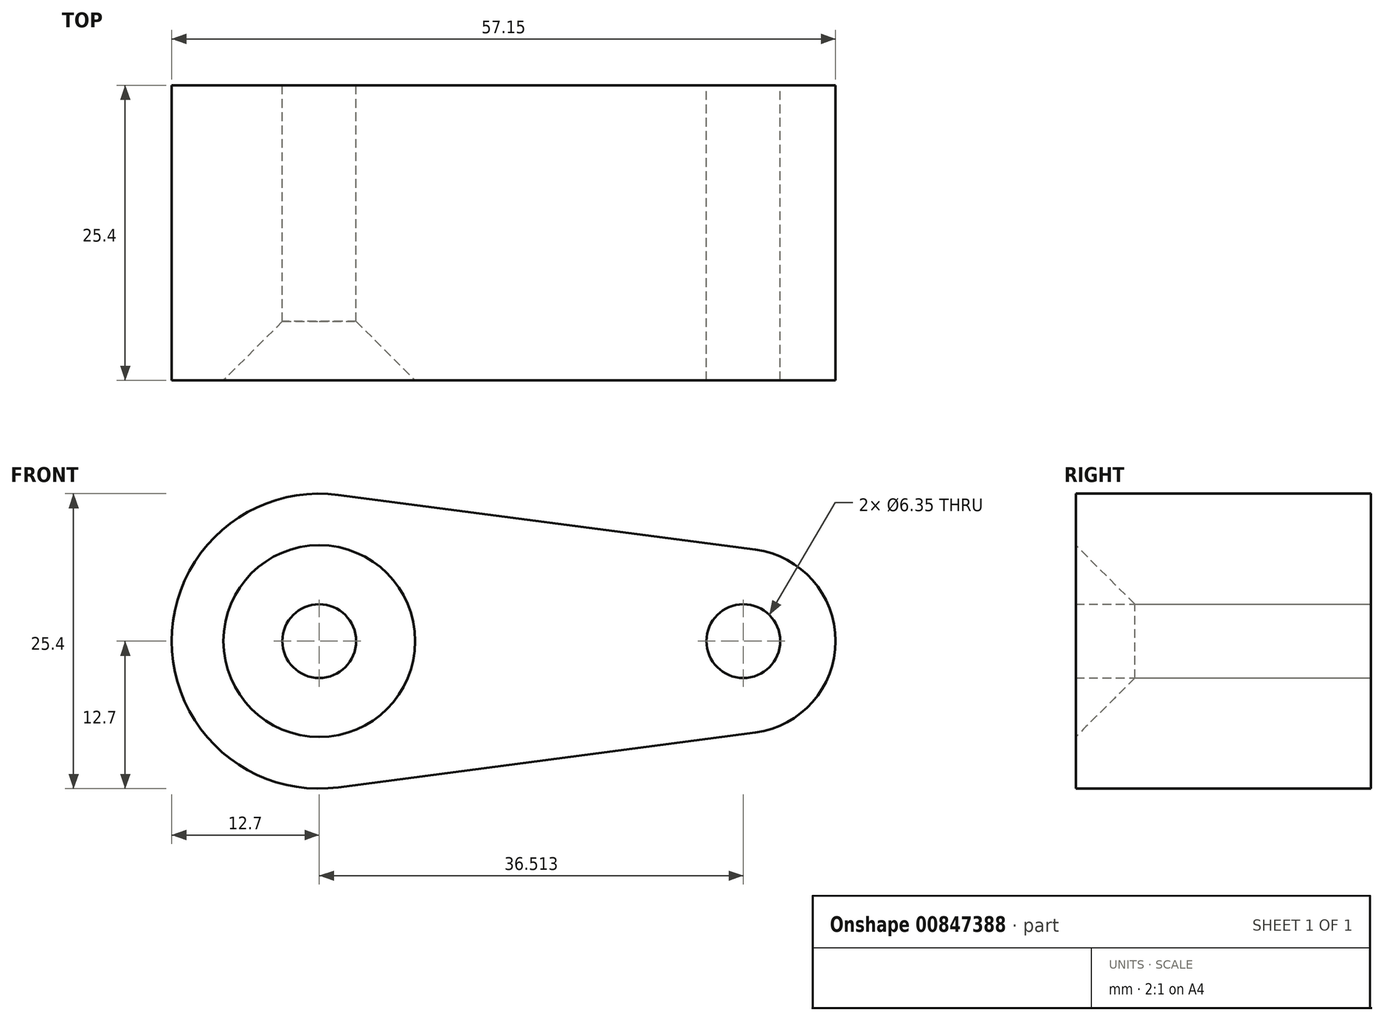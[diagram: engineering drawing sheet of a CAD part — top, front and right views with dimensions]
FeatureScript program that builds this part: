
annotation { "Feature Type Name" : "Feature", "Feature Type Description" : "" }
export const myFeature = defineFeature(function(context is Context, id is Id, definition is map)
    precondition{}
    {
        {
            var Q0;
            Q0=qCreatedBy(makeId("Front.planeOp"),FACE);
            var sketch = newSketch(context, id + "F0", { "sketchPlane" : qUnion([Q0])});
            skLineSegment(sketch, "E0.bottom", {"start": v(-46.46, 87.45) * mm, "end": v(47.03, 87.45) * mm});
            skLineSegment(sketch, "E0.top", {"start": v(-46.46, -90.1) * mm, "end": v(47.03, -90.1) * mm});
            skLineSegment(sketch, "E0.left", {"start": v(-46.46, 87.45) * mm, "end": v(-46.46, -90.1) * mm});
            skLineSegment(sketch, "E0.right", {"start": v(47.03, 87.45) * mm, "end": v(47.03, -90.1) * mm});
            skCircle(sketch, "E1", {"center": v(0, 0) * mm, "radius": 7.39 * mm});
            skSolve(sketch);
        }
        {
            var Q0;
            Q0=makeQuery(id+"F0.imprint","IMPRINT",FACE,{"disambiguationData":[TD([[makeQuery(id+"F0.imprint","IMPRINT",EDGE,{"derivedFrom":sQuery(id+"F0.wireOp",EDGE,"E0.bottom")}),-1.0]])]});
            extrude(context, id + "F1", {"entities" : qUnion([Q0]), "depth" : 25.4 * mm, "offsetDistance" : 25.4 * mm});
        }
        {
            var Q0;
            Q0=makeQuery(id+"F1.opExtrude","CAP_FACE",FACE,{"disambiguationData":[OSD([sQuery(id+"F0.wireOp",EDGE,"E0.bottom"),sQuery(id+"F0.wireOp",EDGE,"E0.top"),sQuery(id+"F0.wireOp",EDGE,"E0.left"),sQuery(id+"F0.wireOp",EDGE,"E0.right"),sQuery(id+"F0.wireOp",EDGE,"E1")])],"isStart":false});
            var sketch = newSketch(context, id + "F2", { "sketchPlane" : qUnion([Q0])});
            skCircle(sketch, "E2.0", {"center": v(0, 0) * mm, "radius": 7.39 * mm});
            skCircle(sketch, "E3.0", {"center": v(0, 0) * mm, "radius": 26.44 * mm});
            skSolve(sketch);
        }
        {
            var Q0;
            Q0=sQuery(id+"F2.wireOp",EDGE,"E3.0");
            var Q1;
            Q1=sQuery(id+"F2.wireOp",EDGE,"E2.0");
            extrude(context, id + "F3", {"bodyType" : ToolBodyType.SURFACE, "surfaceEntities" : qUnion([Q0, Q1]), "depth" : 25.4 * mm, "offsetDistance" : 25.4 * mm});
        }
        {
            var Q0;
            Q0=makeQuery(id+"F1.opExtrude","SWEPT_BODY",BODY,{"disambiguationData":[OSD([sQuery(id+"F0.wireOp",EDGE,"E0.bottom"),sQuery(id+"F0.wireOp",EDGE,"E0.top"),sQuery(id+"F0.wireOp",EDGE,"E0.left"),sQuery(id+"F0.wireOp",EDGE,"E0.right"),sQuery(id+"F0.wireOp",EDGE,"E1")])]});
            var Q1;
            Q1=makeQuery(id+"F3.opExtrude","SWEPT_BODY",BODY,{"disambiguationData":[OSD([sQuery(id+"F2.wireOp",EDGE,"E2.0")])]});
            var Q2;
            Q2=makeQuery(id+"F3.opExtrude","SWEPT_BODY",BODY,{"disambiguationData":[OSD([sQuery(id+"F2.wireOp",EDGE,"E3.0")])]});
            deleteBodies(context, id + "F4", {"entities" : qUnion([Q0, Q1, Q2])});
        }
        {
            var Q0;
            Q0=qCreatedBy(makeId("Front.planeOp"),FACE);
            var sketch = newSketch(context, id + "F5", { "sketchPlane" : qUnion([Q0])});
            skCircle(sketch, "E4", {"center": v(0, 0) * mm, "radius": 12.7 * mm});
            skCircle(sketch, "E5", {"center": v(36.51, 0) * mm, "radius": 7.94 * mm});
            skLineSegment(sketch, "E6", {"start": v(1.66, 12.6) * mm, "end": v(37.55, 7.87) * mm});
            skLineSegment(sketch, "E7", {"start": v(1.66, -12.6) * mm, "end": v(37.55, -7.87) * mm});
            skCircle(sketch, "E8", {"center": v(0, 0) * mm, "radius": 3.18 * mm});
            skCircle(sketch, "E9", {"center": v(36.51, 0) * mm, "radius": 3.18 * mm});
            skSolve(sketch);
        }
        {
            var Q0;
            Q0 = qSketchRegion(id + "F5", true);
            extrude(context, id + "F6", {"entities" : qUnion([Q0]), "depth" : 25.4 * mm, "offsetDistance" : 25.4 * mm});
        }
        {
            var Q0;
            Q0=makeQuery(id+"F6.opExtrude","CAP_EDGE",EDGE,{"disambiguationData":[OSD([sQuery(id+"F5.wireOp",EDGE,"E8")])],"isStart":false});
            chamfer(context, id + "F7", {"entities" : qUnion([Q0]), "width" : 5.08 * mm, "tangentPropagation" : true});
        }
    });
